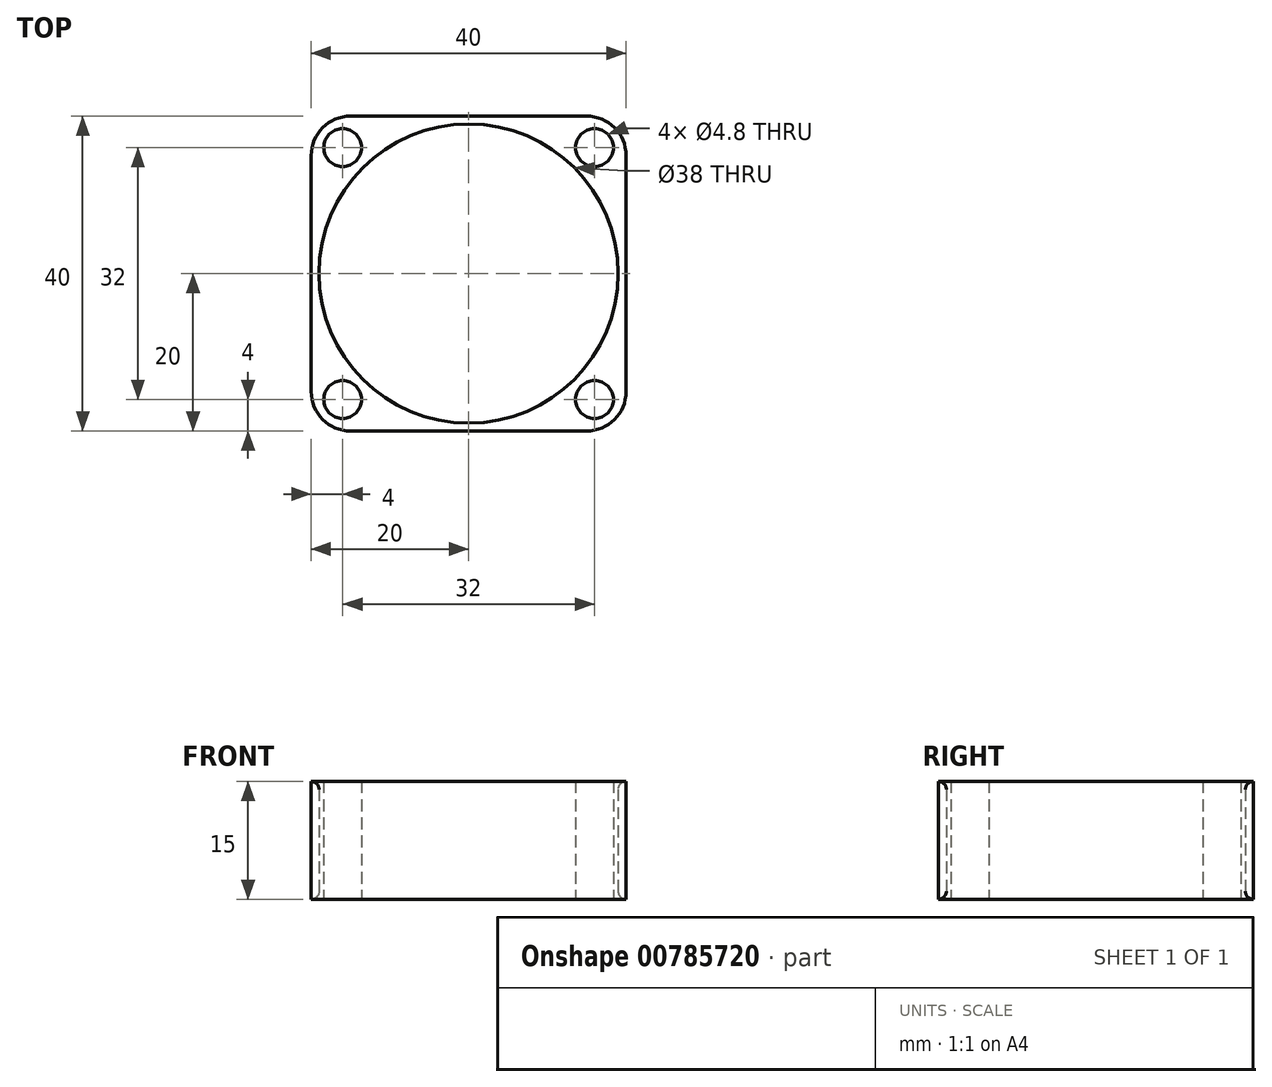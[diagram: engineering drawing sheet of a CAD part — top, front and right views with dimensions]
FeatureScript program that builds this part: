
annotation { "Feature Type Name" : "Feature", "Feature Type Description" : "" }
export const myFeature = defineFeature(function(context is Context, id is Id, definition is map)
    precondition{}
    {
        {
            var Q0;
            Q0=qCreatedBy(makeId("Top.planeOp"),FACE);
            var sketch = newSketch(context, id + "F0", { "sketchPlane" : qUnion([Q0])});
            skCircle(sketch, "E0", {"center": v(0, 0) * mm, "radius": 19 * mm});
            skLineSegment(sketch, "E1.bottom", {"start": v(-20, 20) * mm, "end": v(20, 20) * mm});
            skLineSegment(sketch, "E1.top", {"start": v(-20, -20) * mm, "end": v(20, -20) * mm});
            skLineSegment(sketch, "E1.left", {"start": v(-20, 20) * mm, "end": v(-20, -20) * mm});
            skLineSegment(sketch, "E1.right", {"start": v(20, 20) * mm, "end": v(20, -20) * mm});
            skCircle(sketch, "E2", {"center": v(-16, 16) * mm, "radius": 2.4 * mm});
            skCircle(sketch, "E3.0.1.0", {"center": v(-16, -16) * mm, "radius": 2.4 * mm});
            skCircle(sketch, "E3.1.0.0", {"center": v(16, 16) * mm, "radius": 2.4 * mm});
            skCircle(sketch, "E3.1.1.0", {"center": v(16, -16) * mm, "radius": 2.4 * mm});
            skLineSegment(sketch, "E3.direction1", {"start": v(-16, 16) * mm, "end": v(16, 16) * mm, "construction": true});
            skLineSegment(sketch, "E3.direction2", {"start": v(-16, 16) * mm, "end": v(-16, -16) * mm, "construction": true});
            skSolve(sketch);
        }
        {
            var Q0;
            Q0=makeQuery(id+"F0.imprint","IMPRINT",FACE,{"disambiguationData":[TD([[makeQuery(id+"F0.imprint","IMPRINT",EDGE,{"derivedFrom":sQuery(id+"F0.wireOp",EDGE,"E0")}),-1.0]])]});
            extrude(context, id + "F1", {"entities" : qUnion([Q0]), "depth" : 15 * mm, "offsetDistance" : 25 * mm});
        }
        {
            var Q0;
            Q0=makeQuery(id+"F1.opExtrude","SWEPT_EDGE",EDGE,{"disambiguationData":[OSD([sQuery(id+"F0.wireOp",EDGE,"E1.bottom"),sQuery(id+"F0.wireOp",EDGE,"E1.right")])]});
            var Q1;
            Q1=makeQuery(id+"F1.opExtrude","SWEPT_EDGE",EDGE,{"disambiguationData":[OSD([sQuery(id+"F0.wireOp",EDGE,"E1.top"),sQuery(id+"F0.wireOp",EDGE,"E1.right")])]});
            var Q2;
            Q2=makeQuery(id+"F1.opExtrude","SWEPT_EDGE",EDGE,{"disambiguationData":[OSD([sQuery(id+"F0.wireOp",EDGE,"E1.bottom"),sQuery(id+"F0.wireOp",EDGE,"E1.left")])]});
            var Q3;
            Q3=makeQuery(id+"F1.opExtrude","SWEPT_EDGE",EDGE,{"disambiguationData":[OSD([sQuery(id+"F0.wireOp",EDGE,"E1.top"),sQuery(id+"F0.wireOp",EDGE,"E1.left")])]});
            fillet(context, id + "F2", {"entities" : qUnion([Q0, Q1, Q2, Q3]), "radius" : 5 * mm, "tangentPropagation" : true, "allowEdgeOverflow" : false});
        }
        {
            var Q0;
            Q0=makeQuery(id+"F1.opExtrude","CAP_EDGE",EDGE,{"disambiguationData":[OSD([sQuery(id+"F0.wireOp",EDGE,"E0")])],"isStart":false});
            var Q1;
            Q1=makeQuery(id+"F1.opExtrude","CAP_EDGE",EDGE,{"disambiguationData":[OSD([sQuery(id+"F0.wireOp",EDGE,"E0")])],"isStart":true});
            fillet(context, id + "F3", {"entities" : qUnion([Q0, Q1]), "radius" : 1 * mm, "tangentPropagation" : true, "allowEdgeOverflow" : false});
        }
    });
